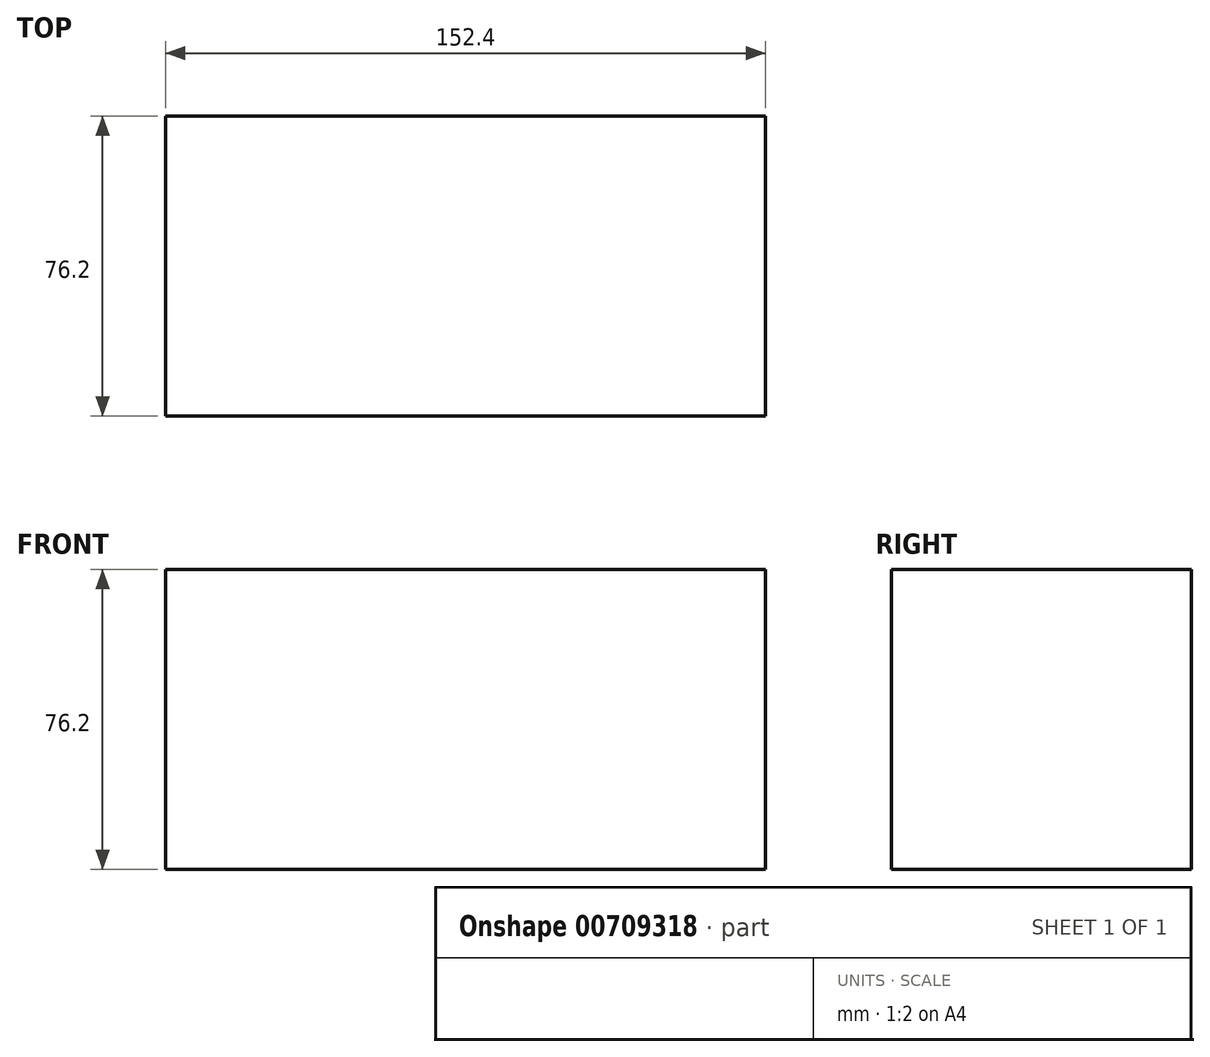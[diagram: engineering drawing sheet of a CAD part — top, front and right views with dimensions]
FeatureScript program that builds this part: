
annotation { "Feature Type Name" : "Feature", "Feature Type Description" : "" }
export const myFeature = defineFeature(function(context is Context, id is Id, definition is map)
    precondition{}
    {
        {
            var Q0;
            Q0=qCreatedBy(makeId("Front.planeOp"),FACE);
            var sketch = newSketch(context, id + "F0", { "sketchPlane" : qUnion([Q0])});
            skLineSegment(sketch, "E0.bottom", {"start": v(76.2, -38.1) * mm, "end": v(-76.2, -38.1) * mm});
            skLineSegment(sketch, "E0.top", {"start": v(76.2, 38.1) * mm, "end": v(-76.2, 38.1) * mm});
            skLineSegment(sketch, "E0.left", {"start": v(76.2, -38.1) * mm, "end": v(76.2, 38.1) * mm});
            skLineSegment(sketch, "E0.right", {"start": v(-76.2, -38.1) * mm, "end": v(-76.2, 38.1) * mm});
            skPoint(sketch, "E0.middle", {"position": v(0, 0) * mm});
            skSolve(sketch);
        }
        {
            var Q0;
            Q0 = qSketchRegion(id + "F0", true);
            extrude(context, id + "F1", {"entities" : qUnion([Q0]), "depth" : 76.2 * mm, "offsetDistance" : 25.4 * mm});
        }
    });
